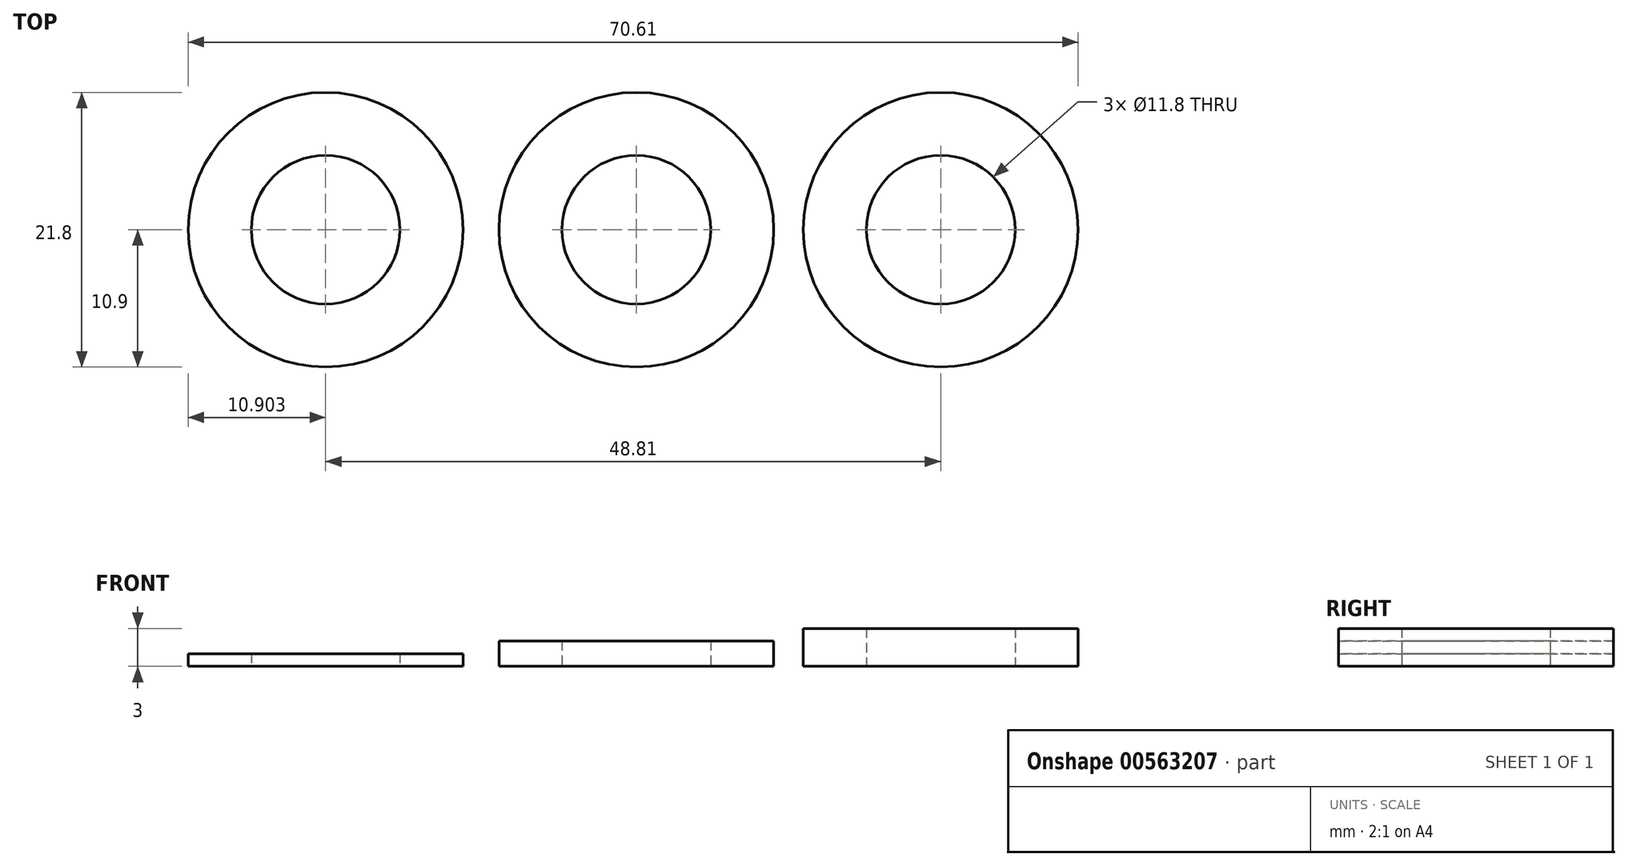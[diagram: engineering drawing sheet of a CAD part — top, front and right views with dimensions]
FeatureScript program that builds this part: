
annotation { "Feature Type Name" : "Feature", "Feature Type Description" : "" }
export const myFeature = defineFeature(function(context is Context, id is Id, definition is map)
    precondition{}
    {
        {
            var Q0;
            Q0=qCreatedBy(makeId("Top.planeOp"),FACE);
            var sketch = newSketch(context, id + "F0", { "sketchPlane" : qUnion([Q0])});
            skCircle(sketch, "E0", {"center": v(-61.18, 0) * mm, "radius": 5.9 * mm});
            skCircle(sketch, "E1.0", {"center": v(-61.18, 0) * mm, "radius": 10.9 * mm});
            skCircle(sketch, "E2", {"center": v(14.8, 0) * mm, "radius": 5.9 * mm});
            skCircle(sketch, "E3.0", {"center": v(14.8, 0) * mm, "radius": 10.9 * mm});
            skCircle(sketch, "E4", {"center": v(-10.86, 0) * mm, "radius": 5.9 * mm});
            skCircle(sketch, "E5.0", {"center": v(-10.86, 0) * mm, "radius": 10.9 * mm});
            skCircle(sketch, "E6", {"center": v(-37.03, 0) * mm, "radius": 5.9 * mm});
            skCircle(sketch, "E7.0", {"center": v(-37.03, 0) * mm, "radius": 10.9 * mm});
            skCircle(sketch, "E8", {"center": v(-85.84, 0) * mm, "radius": 5.9 * mm});
            skCircle(sketch, "E9.0", {"center": v(-85.84, 0) * mm, "radius": 10.9 * mm});
            skSolve(sketch);
        }
        {
            var Q0;
            Q0=makeQuery(id+"F0.imprint","IMPRINT",FACE,{"disambiguationData":[TD([[makeQuery(id+"F0.imprint","IMPRINT",EDGE,{"derivedFrom":sQuery(id+"F0.wireOp",EDGE,"E8")}),-1.0]])]});
            extrude(context, id + "F1", {"entities" : qUnion([Q0]), "depth" : 1 * mm, "offsetDistance" : 25 * mm});
        }
        {
            var Q0;
            Q0=makeQuery(id+"F0.imprint","IMPRINT",FACE,{"disambiguationData":[TD([[makeQuery(id+"F0.imprint","IMPRINT",EDGE,{"derivedFrom":sQuery(id+"F0.wireOp",EDGE,"E0")}),-1.0]])]});
            extrude(context, id + "F2", {"entities" : qUnion([Q0]), "depth" : 2 * mm, "offsetDistance" : 25 * mm});
        }
        {
            var Q0;
            Q0=makeQuery(id+"F0.imprint","IMPRINT",FACE,{"disambiguationData":[TD([[makeQuery(id+"F0.imprint","IMPRINT",EDGE,{"derivedFrom":sQuery(id+"F0.wireOp",EDGE,"E6")}),-1.0]])]});
            extrude(context, id + "F3", {"entities" : qUnion([Q0]), "depth" : 3 * mm, "offsetDistance" : 25 * mm});
        }
    });
